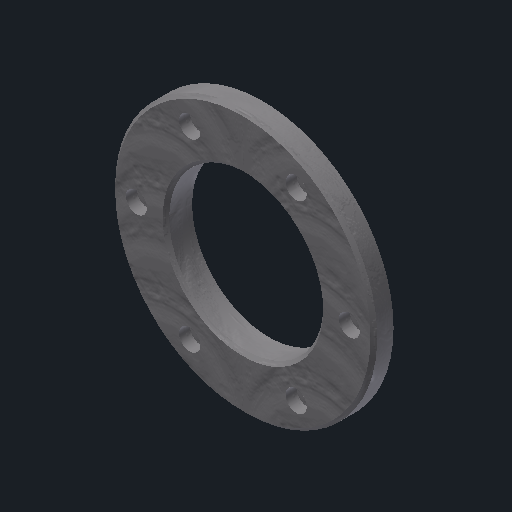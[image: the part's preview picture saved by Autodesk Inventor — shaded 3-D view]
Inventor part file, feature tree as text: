
AUTODESK INVENTOR PART (.ipt)
format: ipt  version: 2022 (Build 260153000, 153)  size: 194,048 bytes
history: native  units: mm
features: sketch x3, plane x2, extrude x2, chamfer x2, reference x2, other x2, hole x1
ambient origin geometry x8: Origin, YZ Plane, XZ Plane, XY Plane, X Axis, Y Axis, Z Axis, Center Point
bodies: Body1 (feature_tree)
feature tree (14):
  sketch  "Sketch1"  dims[d0=47.0mm d26=10.0mm d27=0.0mm]
  plane  "Work Plane3"
  extrude  "Extrusion3"  Depth=10.0mm TaperAngle=0.0deg
  sketch  "Sketch4"  dims[d28=10.0mm d29=0.0mm d30=2.0mm d31=2.0mm d32=45.0deg d33=1.0mm d34=2.0mm d35=45.0deg]
  plane  "Work Plane4"
  extrude  "Extrusion4"  Depth=2.0mm TaperAngle=45.0deg
  chamfer  "Chamfer4"  Distance=1.0mm Angle=45.0deg
  chamfer  "Chamfer5"  Distance=60.0mm Angle=360.0deg
  hole  "Hole2"  [1 undecoded]
  reference  "Reference1"
  reference  "Reference3"
  sketch  "Sketch5"  dims[d36=65.0mm d37=60.0mm d39=360.0deg d41=3.4mm d42=6.0mm d43=6.5mm d44=3.4mm d45=90.0deg d46=8.0mm d47=20.594885mm]
  other  "Assembly2.iam"
  other  "Soporte:1"
note: 1 required parameter value undecoded (feature->parameter linkage not recoverable at this tier; creation-order binding heuristic only, values carry confidence <= 0.55)
